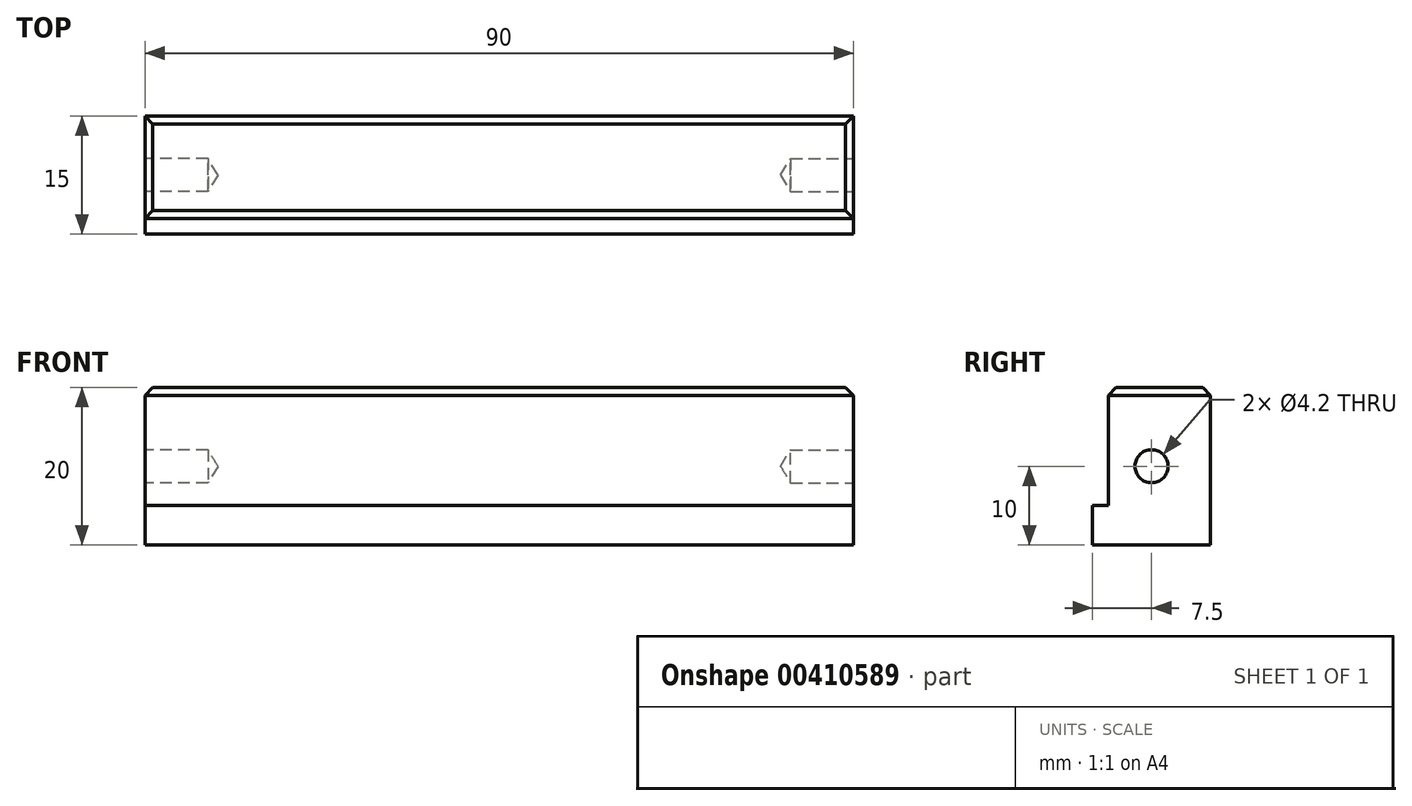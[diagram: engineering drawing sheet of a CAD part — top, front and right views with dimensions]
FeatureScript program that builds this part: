
annotation { "Feature Type Name" : "Feature", "Feature Type Description" : "" }
export const myFeature = defineFeature(function(context is Context, id is Id, definition is map)
    precondition{}
    {
        {
            var Q0;
            Q0=qCreatedBy(makeId("Top.planeOp"),FACE);
            var sketch = newSketch(context, id + "F0", { "sketchPlane" : qUnion([Q0])});
            skLineSegment(sketch, "E0.bottom", {"start": v(0, 0) * mm, "end": v(90, 0) * mm});
            skLineSegment(sketch, "E0.top", {"start": v(0, 15) * mm, "end": v(90, 15) * mm});
            skLineSegment(sketch, "E0.left", {"start": v(0, 0) * mm, "end": v(0, 15) * mm});
            skLineSegment(sketch, "E0.right", {"start": v(90, 0) * mm, "end": v(90, 15) * mm});
            skSolve(sketch);
        }
        {
            var Q0;
            Q0 = qSketchRegion(id + "F0", true);
            extrude(context, id + "F1", {"entities" : qUnion([Q0]), "depth" : 5 * mm});
        }
        {
            var Q0;
            Q0=makeQuery(id+"F1.opExtrude","CAP_FACE",FACE,{"disambiguationData":[OSD([sQuery(id+"F0.wireOp",EDGE,"E0.bottom"),sQuery(id+"F0.wireOp",EDGE,"E0.top"),sQuery(id+"F0.wireOp",EDGE,"E0.left"),sQuery(id+"F0.wireOp",EDGE,"E0.right")])],"isStart":false});
            var sketch = newSketch(context, id + "F2", { "sketchPlane" : qUnion([Q0])});
            skLineSegment(sketch, "E1.bottom", {"start": v(90, 15) * mm, "end": v(0, 15) * mm});
            skLineSegment(sketch, "E1.top", {"start": v(90, 2) * mm, "end": v(0, 2) * mm});
            skLineSegment(sketch, "E1.left", {"start": v(90, 15) * mm, "end": v(90, 2) * mm});
            skLineSegment(sketch, "E1.right", {"start": v(0, 15) * mm, "end": v(0, 2) * mm});
            skSolve(sketch);
        }
        {
            var Q0;
            Q0 = qSketchRegion(id + "F2", true);
            extrude(context, id + "F3", {"entities" : qUnion([Q0]), "operationType" : NewBodyOperationType.ADD, "depth" : 15 * mm});
        }
        {
            var Q0;
            Q0=makeQuery(id+"F3.boolean.opBoolean","MERGE",FACE,{"derivedFrom":[makeQuery(id+"F1.opExtrude","SWEPT_FACE",FACE,{"disambiguationData":[OSD([sQuery(id+"F0.wireOp",EDGE,"E0.right")])]}),makeQuery(id+"F3.opExtrude","SWEPT_FACE",FACE,{"disambiguationData":[OSD([sQuery(id+"F2.wireOp",EDGE,"E1.left")])]})]});
            var sketch = newSketch(context, id + "F4", { "sketchPlane" : qUnion([Q0])});
            skPoint(sketch, "E2", {"position": v(7.5, 10) * mm});
            skSolve(sketch);
        }
        {
            var Q0;
            Q0=sQuery(id+"F4.wireOp",VERTEX,"E2");
            var Q1;
            Q1=makeQuery(id+"F1.opExtrude","SWEPT_BODY",BODY,{"disambiguationData":[OSD([sQuery(id+"F0.wireOp",EDGE,"E0.bottom"),sQuery(id+"F0.wireOp",EDGE,"E0.top"),sQuery(id+"F0.wireOp",EDGE,"E0.left"),sQuery(id+"F0.wireOp",EDGE,"E0.right")])]});
            hole(context, id + "F5", {"style" : HoleStyle.SIMPLE, "endStyle" : HoleEndStyle.BLIND, "standardTappedOrClearance" : lookupTablePath({ "standard" : "ISO", "engagement" : "75%", "pitch" : "0.8 mm", "size" : "M5", "type" : "Tapped" }), "standardBlindInLast" : lookupTablePath({ "standard" : "ISO", "engagement" : "75%", "pitch" : "0.8 mm", "size" : "M5", "type" : "Tapped" }), "holeDiameter" : 4.2 * mm, "showTappedDepth" : true, "holeDepth" : 8 * mm, "isTappedThrough" : true, "tappedDepth" : 5.6 * mm, "tapClearance" : 3, "locations" : qUnion([Q0]), "scope" : qUnion([Q1]), "majorDiameter" : 5 * mm});
        }
        {
            var Q0;
            Q0=makeQuery(id+"F3.boolean.opBoolean","MERGE",FACE,{"derivedFrom":[makeQuery(id+"F1.opExtrude","SWEPT_FACE",FACE,{"disambiguationData":[OSD([sQuery(id+"F0.wireOp",EDGE,"E0.left")])]}),makeQuery(id+"F3.opExtrude","SWEPT_FACE",FACE,{"disambiguationData":[OSD([sQuery(id+"F2.wireOp",EDGE,"E1.right")])]})]});
            var sketch = newSketch(context, id + "F6", { "sketchPlane" : qUnion([Q0])});
            skPoint(sketch, "E3", {"position": v(-7.5, 10) * mm});
            skSolve(sketch);
        }
        {
            var Q0;
            Q0=sQuery(id+"F6.wireOp",VERTEX,"E3");
            var Q1;
            Q1=makeQuery(id+"F1.opExtrude","SWEPT_BODY",BODY,{"disambiguationData":[OSD([sQuery(id+"F0.wireOp",EDGE,"E0.bottom"),sQuery(id+"F0.wireOp",EDGE,"E0.top"),sQuery(id+"F0.wireOp",EDGE,"E0.left"),sQuery(id+"F0.wireOp",EDGE,"E0.right")])]});
            hole(context, id + "F7", {"style" : HoleStyle.SIMPLE, "endStyle" : HoleEndStyle.BLIND, "standardTappedOrClearance" : lookupTablePath({ "standard" : "ISO", "engagement" : "75%", "pitch" : "0.8 mm", "size" : "M5", "type" : "Tapped" }), "standardBlindInLast" : lookupTablePath({ "standard" : "ISO", "engagement" : "75%", "pitch" : "0.8 mm", "size" : "M5", "type" : "Tapped" }), "holeDiameter" : 4.2 * mm, "showTappedDepth" : true, "holeDepth" : 8 * mm, "isTappedThrough" : true, "tappedDepth" : 5.6 * mm, "tapClearance" : 3, "locations" : qUnion([Q0]), "scope" : qUnion([Q1]), "majorDiameter" : 5 * mm});
        }
        {
            var Q0;
            Q0=makeQuery(id+"F3.opExtrude","CAP_EDGE",EDGE,{"disambiguationData":[OSD([sQuery(id+"F2.wireOp",EDGE,"E1.top")])],"isStart":false});
            var Q1;
            Q1=makeQuery(id+"F3.opExtrude","CAP_EDGE",EDGE,{"disambiguationData":[OSD([sQuery(id+"F2.wireOp",EDGE,"E1.left")])],"isStart":false});
            var Q2;
            Q2=makeQuery(id+"F3.opExtrude","CAP_EDGE",EDGE,{"disambiguationData":[OSD([sQuery(id+"F2.wireOp",EDGE,"E1.bottom")])],"isStart":false});
            var Q3;
            Q3=makeQuery(id+"F3.opExtrude","CAP_EDGE",EDGE,{"disambiguationData":[OSD([sQuery(id+"F2.wireOp",EDGE,"E1.right")])],"isStart":false});
            chamfer(context, id + "F8", {"entities" : qUnion([Q0, Q1, Q2, Q3]), "width" : 1 * mm, "tangentPropagation" : true});
        }
    });
